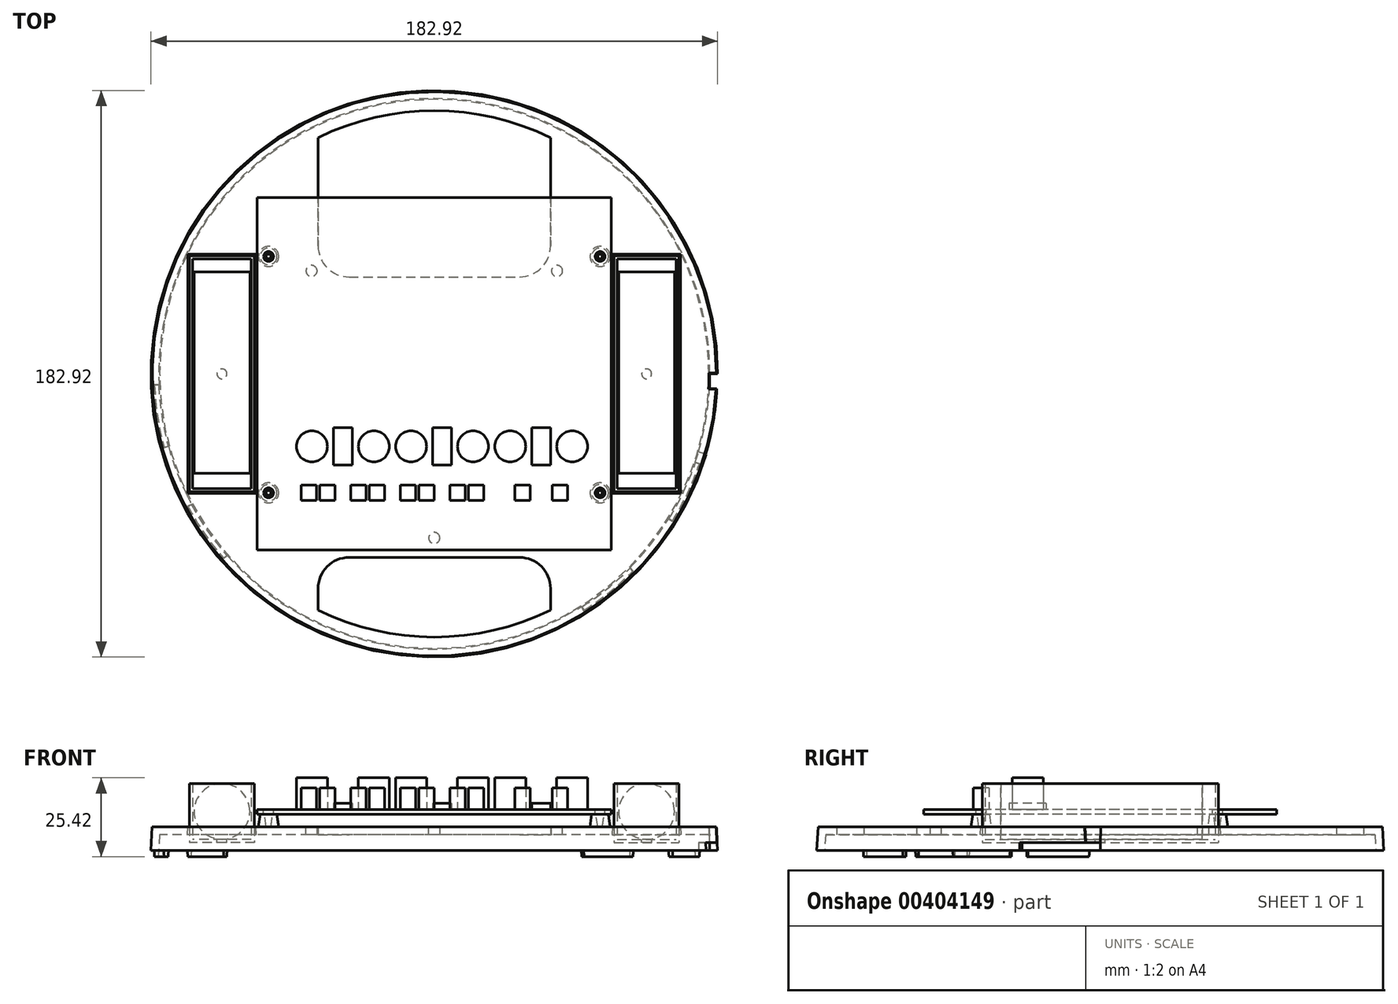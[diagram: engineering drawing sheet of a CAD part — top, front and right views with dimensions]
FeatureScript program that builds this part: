
annotation { "Feature Type Name" : "Feature", "Feature Type Description" : "" }
export const myFeature = defineFeature(function(context is Context, id is Id, definition is map)
    precondition{}
    {
        {
            assignVariable(context, id + "F0", {"name" : "h_env", "anyValue" : 230});
        }
        {
            var Q0;
            Q0=qCreatedBy(makeId("Top.planeOp"),FACE);
            var sketch = newSketch(context, id + "F1", { "sketchPlane" : qUnion([Q0])});
            skCircle(sketch, "E0", {"center": v(0, 0) * mm, "radius": 94 * mm});
            skSolve(sketch);
        }
        {
            var Q0;
            Q0=qCreatedBy(makeId("Top.planeOp"),FACE);
            cPlane(context, id + "F2", {"entities" : qUnion([Q0]), "cplaneType" : CPlaneType.OFFSET, "offset" : (getVariable(context, 'h_env')) * mm, "width" : 152.4 * mm, "height" : 152.4 * mm});
        }
        {
            var Q0;
            Q0=makeQuery(id+"F1.imprint","IMPRINT",FACE,{"disambiguationData":[TD([[makeQuery(id+"F1.imprint","IMPRINT",EDGE,{"derivedFrom":sQuery(id+"F1.wireOp",EDGE,"E0")}),1.0]])]});
            var Q1;
            Q1=sQuery(id+"F1.wireOp",EDGE,"E0");
            var Q2;
            Q2=qCreatedBy(id+"F2.planeOp",FACE);
            extrude(context, id + "F3", {"entities" : qUnion([Q0]), "bodyType" : ToolBodyType.SURFACE, "surfaceEntities" : qUnion([Q1]), "endBound" : BoundingType.UP_TO_SURFACE, "endBoundEntityFace" : qUnion([Q2]), "depth" : 25.4 * mm});
        }
        {
            var Q0;
            Q0=qCreatedBy(makeId("Right.planeOp"),FACE);
            var sketch = newSketch(context, id + "F4", { "sketchPlane" : qUnion([Q0])});
            skLineSegment(sketch, "E1", {"start": v(0, 0) * mm, "end": v(0, 230) * mm, "construction": true});
            skSolve(sketch);
        }
        {
            assignVariable(context, id + "F5", {"name" : "t", "anyValue" : 2.54});
        }
        {
            assignVariable(context, id + "F6", {"name" : "h_primary", "anyValue" : 19.05});
        }
        {
            assignVariable(context, id + "F7", {"name" : "draft", "anyValue" : 3});
        }
        {
            var Q0;
            Q0=qCreatedBy(id+"F2.planeOp",FACE);
            cPlane(context, id + "F8", {"entities" : qUnion([Q0]), "cplaneType" : CPlaneType.OFFSET, "offset" : (getVariable(context, 'h_primary')) * mm, "oppositeDirection" : true, "width" : 152.4 * mm, "height" : 152.4 * mm});
        }
        {
            var Q0;
            Q0=qCreatedBy(id+"F8.planeOp",FACE);
            var sketch = newSketch(context, id + "F9", { "sketchPlane" : qUnion([Q0])});
            skCircle(sketch, "E2", {"center": v(0, 0) * mm, "radius": 91.46 * mm});
            skSolve(sketch);
        }
        {
            var Q0;
            Q0=makeQuery(id+"F9.imprint","IMPRINT",FACE,{"disambiguationData":[TD([[makeQuery(id+"F9.imprint","IMPRINT",EDGE,{"derivedFrom":sQuery(id+"F9.wireOp",EDGE,"E2")}),1.0]])]});
            extrude(context, id + "F10", {"entities" : qUnion([Q0]), "depth" : (3 * getVariable(context, 't')) * mm, "hasDraft" : true, "draftAngle" : (getVariable(context, 'draft')) * degree, "draftPullDirection" : true});
        }
        {
            var Q0;
            Q0=makeQuery(id+"F10.opExtrude","CAP_FACE",FACE,{"disambiguationData":[OSD([sQuery(id+"F9.wireOp",EDGE,"E2")])],"isStart":true});
            shell(context, id + "F11", {"entities" : qUnion([Q0]), "thickness" : (getVariable(context, 't')) * mm});
        }
        {
            var Q0;
            Q0=makeQuery(id+"F10.opExtrude","CAP_FACE",FACE,{"disambiguationData":[OSD([sQuery(id+"F9.wireOp",EDGE,"E2")])],"isStart":true});
            var sketch = newSketch(context, id + "F12", { "sketchPlane" : qUnion([Q0])});
            skLineSegment(sketch, "E3", {"start": v(0, 0) * mm, "end": v(88.34, 23.67) * mm, "construction": true});
            skLineSegment(sketch, "E4", {"start": v(0, 0) * mm, "end": v(91.46, 0) * mm, "construction": true});
            skLineSegment(sketch, "E5", {"start": v(0, 0) * mm, "end": v(87.7, 25.98) * mm, "construction": true});
            skCircle(sketch, "E6.0", {"center": v(0, 0) * mm, "radius": 88.65 * mm});
            skArc(sketch, "E7", {"start": v(88.65, 0) * mm, "mid": v(87.73, 12.72) * mm, "end": v(85, 25.18) * mm});
            skLineSegment(sketch, "E8", {"start": v(87.7, 25.98) * mm, "end": v(85, 25.18) * mm});
            skLineSegment(sketch, "E9", {"start": v(91.46, 0) * mm, "end": v(88.65, 0) * mm});
            skSolve(sketch);
        }
        {
            var Q0;
            {var subQ0=sQuery(id+"F12.wireOp",EDGE,"E8");var subQ1=sQuery(id+"F9.wireOp",EDGE,"E2");var subQ2=makeQuery(id+"F10.opExtrude","CAP_EDGE",EDGE,{"disambiguationData":[OSD([subQ1])],"isStart":true});var subQ3=makeQuery(id+"F12.imprint","INTERSECT",VERTEX,{"derivedFrom":[subQ2,subQ0]});Q0=makeQuery(id+"F12.imprint","IMPRINT",FACE,{"disambiguationData":[TD([[makeQuery(id+"F12.imprint","IMPRINT",EDGE,{"disambiguationData":[TD([[subQ3,-1.0]])],"derivedFrom":subQ2}),-1.0]])]});}
            var Q1;
            {var subQ0=sQuery(id+"F12.wireOp",EDGE,"E8");var subQ1=sQuery(id+"F12.wireOp",EDGE,"E6.0");var subQ2=makeQuery(id+"F12.imprint","INTERSECT",VERTEX,{"derivedFrom":[subQ1,subQ0]});Q1=makeQuery(id+"F12.imprint","IMPRINT",FACE,{"disambiguationData":[TD([[makeQuery(id+"F12.imprint","IMPRINT",EDGE,{"disambiguationData":[TD([[subQ2,-1.0]])],"derivedFrom":subQ1}),1.0]])]});}
            extrude(context, id + "F13", {"entities" : qUnion([Q0, Q1]), "operationType" : NewBodyOperationType.REMOVE, "oppositeDirection" : true, "depth" : (getVariable(context, 't')) * mm});
        }
        {
            var Q0;
            Q0=makeQuery(id+"F13.boolean.opBoolean","COPY",FACE,{"derivedFrom":makeQuery(id+"F13.opExtrude","CAP_FACE",FACE,{"disambiguationData":[OSD([sQuery(id+"F9.wireOp",EDGE,"E2"),sQuery(id+"F12.wireOp",EDGE,"E6.0"),sQuery(id+"F12.wireOp",EDGE,"E8"),sQuery(id+"F12.wireOp",EDGE,"E9")])],"isStart":false})});
            var sketch = newSketch(context, id + "F14", { "sketchPlane" : qUnion([Q0])});
            skArc(sketch, "E10.0", {"start": v(91.33, 0) * mm, "mid": v(90.38, 13.1) * mm, "end": v(87.57, 25.94) * mm});
            skCircle(sketch, "E11.0", {"center": v(0, 0) * mm, "radius": 88.65 * mm});
            skLineSegment(sketch, "E12.0", {"start": v(91.33, 0) * mm, "end": v(88.65, 0) * mm});
            skPoint(sketch, "E13.orphan", {"position": v(88.78, 0) * mm});
            skLineSegment(sketch, "E14", {"start": v(0, 0) * mm, "end": v(91.33, 0) * mm, "construction": true});
            skLineSegment(sketch, "E15", {"start": v(0, 0) * mm, "end": v(91.2, 4.78) * mm, "construction": true});
            skLineSegment(sketch, "E16", {"start": v(91.2, 4.78) * mm, "end": v(88.53, 4.64) * mm});
            skSolve(sketch);
        }
        {
            var Q0;
            {var subQ0=sQuery(id+"F14.wireOp",EDGE,"E12.0");var subQ1=sQuery(id+"F14.wireOp",EDGE,"E10.0");var subQ2=makeQuery(id+"F14.imprint","INTERSECT",VERTEX,{"derivedFrom":[subQ1,subQ0]});Q0=makeQuery(id+"F14.imprint","IMPRINT",FACE,{"disambiguationData":[TD([[makeQuery(id+"F14.imprint","IMPRINT",EDGE,{"disambiguationData":[TD([[subQ2,-1.0]])],"derivedFrom":subQ1}),1.0]])]});}
            var Q1;
            Q1=makeQuery(id+"F10.opExtrude","CAP_FACE",FACE,{"disambiguationData":[OSD([sQuery(id+"F9.wireOp",EDGE,"E2")])],"isStart":false});
            extrude(context, id + "F15", {"entities" : qUnion([Q0]), "operationType" : NewBodyOperationType.REMOVE, "endBound" : BoundingType.UP_TO_SURFACE, "oppositeDirection" : true, "endBoundEntityFace" : qUnion([Q1]), "depth" : 25 * mm, "hasDraft" : true, "draftAngle" : 3 * degree});
        }
        {
            var Q0;
            Q0=makeQuery(id+"F9.imprint","IMPRINT",FACE,{"disambiguationData":[TD([[makeQuery(id+"F9.imprint","IMPRINT",EDGE,{"derivedFrom":sQuery(id+"F9.wireOp",EDGE,"E2")}),1.0]])]});
            var sketch = newSketch(context, id + "F16", { "sketchPlane" : qUnion([Q0])});
            skArc(sketch, "E17", {"start": v(-37.5, 76.28) * mm, "mid": v(0, 85) * mm, "end": v(37.5, 76.28) * mm});
            skLineSegment(sketch, "E18.bottom", {"start": v(-37.5, 76.28) * mm, "end": v(37.5, 76.28) * mm, "construction": true});
            skLineSegment(sketch, "E18.top", {"start": v(-27.5, 31.28) * mm, "end": v(27.5, 31.28) * mm});
            skLineSegment(sketch, "E18.left", {"start": v(-37.5, 76.28) * mm, "end": v(-37.5, 41.28) * mm});
            skLineSegment(sketch, "E18.right", {"start": v(37.5, 76.28) * mm, "end": v(37.5, 41.28) * mm});
            skPoint(sketch, "E19.visualSharp", {"position": v(37.5, 31.28) * mm});
            skArc(sketch, "E19.filletArc", {"start": v(27.5, 31.28) * mm, "mid": v(34.57, 34.2) * mm, "end": v(37.5, 41.28) * mm});
            skPoint(sketch, "E20.visualSharp", {"position": v(-37.5, 31.28) * mm});
            skArc(sketch, "E20.filletArc", {"start": v(-37.5, 41.28) * mm, "mid": v(-34.57, 34.2) * mm, "end": v(-27.5, 31.28) * mm});
            skArc(sketch, "E21", {"start": v(37.5, -76.28) * mm, "mid": v(0, -85) * mm, "end": v(-37.5, -76.28) * mm});
            skLineSegment(sketch, "E22.bottom", {"start": v(-37.5, -76.28) * mm, "end": v(37.5, -76.28) * mm, "construction": true});
            skLineSegment(sketch, "E22.top", {"start": v(-27.5, -59.28) * mm, "end": v(27.5, -59.28) * mm});
            skLineSegment(sketch, "E22.left", {"start": v(-37.5, -76.28) * mm, "end": v(-37.5, -69.28) * mm});
            skLineSegment(sketch, "E22.right", {"start": v(37.5, -76.28) * mm, "end": v(37.5, -69.28) * mm});
            skPoint(sketch, "E23.visualSharp", {"position": v(-37.5, -59.28) * mm});
            skArc(sketch, "E23.filletArc", {"start": v(-27.5, -59.28) * mm, "mid": v(-34.57, -62.2) * mm, "end": v(-37.5, -69.28) * mm});
            skPoint(sketch, "E24.visualSharp", {"position": v(37.5, -59.28) * mm});
            skArc(sketch, "E24.filletArc", {"start": v(37.5, -69.28) * mm, "mid": v(34.57, -62.2) * mm, "end": v(27.5, -59.28) * mm});
            skSolve(sketch);
        }
        {
            var Q0;
            Q0=qSketchRegion(id+"F16",true);
            var Q1;
            Q1=sQuery(id+"F16.wireOp",EDGE,"E18.bottom");
            var Q2;
            Q2=makeQuery(id+"F10.opExtrude","CAP_FACE",FACE,{"disambiguationData":[OSD([sQuery(id+"F9.wireOp",EDGE,"E2")])],"isStart":false});
            extrude(context, id + "F17", {"entities" : qUnion([Q0]), "operationType" : NewBodyOperationType.REMOVE, "surfaceEntities" : qUnion([Q1]), "endBound" : BoundingType.UP_TO_SURFACE, "endBoundEntityFace" : qUnion([Q2]), "depth" : 25 * mm});
        }
        {
            var Q0;
            Q0=qCreatedBy(id+"F8.planeOp",FACE);
            cPlane(context, id + "F18", {"entities" : qUnion([Q0]), "cplaneType" : CPlaneType.OFFSET, "offset" : (5 * getVariable(context, 't') - 1.08) * mm, "width" : 152.4 * mm, "height" : 152.4 * mm});
        }
        {
            assignVariable(context, id + "F19", {"name" : "h_pcb", "anyValue" : 1.6});
        }
        {
            var Q0;
            Q0=qCreatedBy(id+"F18.planeOp",FACE);
            var sketch = newSketch(context, id + "F20", { "sketchPlane" : qUnion([Q0])});
            skLineSegment(sketch, "E25.bottom", {"start": v(-57.15, 56.91) * mm, "end": v(57.15, 56.9) * mm});
            skLineSegment(sketch, "E25.top", {"start": v(-57.15, -56.9) * mm, "end": v(57.15, -56.91) * mm});
            skLineSegment(sketch, "E25.left", {"start": v(-57.15, 56.91) * mm, "end": v(-57.15, -56.91) * mm});
            skLineSegment(sketch, "E25.right", {"start": v(57.15, 56.91) * mm, "end": v(57.15, -56.91) * mm});
            skPoint(sketch, "E26", {"position": v(57.15, 0) * mm});
            skPoint(sketch, "E27", {"position": v(0, 56.9) * mm});
            skSolve(sketch);
        }
        {
            var Q0;
            Q0=makeQuery(id+"F20.imprint","IMPRINT",FACE,{"disambiguationData":[TD([[makeQuery(id+"F20.imprint","IMPRINT",EDGE,{"derivedFrom":sQuery(id+"F20.wireOp",EDGE,"E25.bottom")}),-1.0]])]});
            extrude(context, id + "F21", {"entities" : qUnion([Q0]), "depth" : (getVariable(context, 'h_pcb')) * mm});
        }
        {
            var Q0;
            Q0=makeQuery(id+"F21.opExtrude","CAP_FACE",FACE,{"disambiguationData":[OSD([sQuery(id+"F20.wireOp",EDGE,"E25.bottom"),sQuery(id+"F20.wireOp",EDGE,"E25.top"),sQuery(id+"F20.wireOp",EDGE,"E25.left"),sQuery(id+"F20.wireOp",EDGE,"E25.right")])],"isStart":false});
            var sketch = newSketch(context, id + "F22", { "sketchPlane" : qUnion([Q0])});
            skCircle(sketch, "E28", {"center": v(53.5, 37.9) * mm, "radius": 1.6 * mm});
            skCircle(sketch, "E29.0.1.0", {"center": v(53.5, -38.43) * mm, "radius": 1.6 * mm});
            skCircle(sketch, "E29.1.0.0", {"center": v(-53.5, 37.9) * mm, "radius": 1.6 * mm});
            skCircle(sketch, "E29.1.1.0", {"center": v(-53.5, -38.43) * mm, "radius": 1.6 * mm});
            skLineSegment(sketch, "E29.direction1", {"start": v(53.5, 37.9) * mm, "end": v(-53.5, 37.9) * mm, "construction": true});
            skLineSegment(sketch, "E29.direction2", {"start": v(53.5, 37.9) * mm, "end": v(53.5, -38.43) * mm, "construction": true});
            skSolve(sketch);
        }
        {
            var Q0;
            Q0=qSketchRegion(id+"F22",true);
            extrude(context, id + "F23", {"entities" : qUnion([Q0]), "operationType" : NewBodyOperationType.REMOVE, "endBound" : BoundingType.UP_TO_NEXT, "oppositeDirection" : true, "depth" : 25.4 * mm});
        }
        {
            var Q0;
            Q0=makeQuery(id+"F10.opExtrude","CAP_FACE",FACE,{"disambiguationData":[OSD([sQuery(id+"F9.wireOp",EDGE,"E2")])],"isStart":false});
            var sketch = newSketch(context, id + "F24", { "sketchPlane" : qUnion([Q0])});
            skCircle(sketch, "E30.0", {"center": v(53.5, 37.9) * mm, "radius": 1.6 * mm, "construction": true});
            skCircle(sketch, "E31.0", {"center": v(53.5, -38.43) * mm, "radius": 1.6 * mm, "construction": true});
            skCircle(sketch, "E32.0", {"center": v(-53.5, -38.43) * mm, "radius": 1.6 * mm, "construction": true});
            skCircle(sketch, "E33.0", {"center": v(-53.5, 37.9) * mm, "radius": 1.6 * mm, "construction": true});
            skCircle(sketch, "E34", {"center": v(53.5, 37.9) * mm, "radius": 3.25 * mm});
            skCircle(sketch, "E35", {"center": v(53.5, -38.43) * mm, "radius": 3.25 * mm});
            skCircle(sketch, "E36", {"center": v(-53.5, -38.43) * mm, "radius": 3.25 * mm});
            skCircle(sketch, "E37", {"center": v(-53.5, 37.9) * mm, "radius": 3.25 * mm});
            skCircle(sketch, "E38", {"center": v(53.5, 37.9) * mm, "radius": 0.75 * mm});
            skCircle(sketch, "E39", {"center": v(-53.5, 37.9) * mm, "radius": 0.75 * mm});
            skCircle(sketch, "E40", {"center": v(-53.5, -38.43) * mm, "radius": 0.75 * mm});
            skCircle(sketch, "E41", {"center": v(53.5, -38.43) * mm, "radius": 0.75 * mm});
            skSolve(sketch);
        }
        {
            var Q0;
            Q0=qSketchRegion(id+"F24",true);
            var Q1;
            Q1=sQuery(id+"F24.wireOp",EDGE,"D2eIxqeC-2rqa-4NXI-Nvdh-6eyWbRgn4P1Z");
            var Q2;
            Q2=makeQuery(id+"F21.opExtrude","CAP_FACE",FACE,{"disambiguationData":[OSD([sQuery(id+"F20.wireOp",EDGE,"E25.bottom"),sQuery(id+"F20.wireOp",EDGE,"E25.top"),sQuery(id+"F20.wireOp",EDGE,"E25.left"),sQuery(id+"F20.wireOp",EDGE,"E25.right")])],"isStart":true});
            extrude(context, id + "F25", {"entities" : qUnion([Q0]), "operationType" : NewBodyOperationType.ADD, "surfaceEntities" : qUnion([Q1]), "endBound" : BoundingType.UP_TO_SURFACE, "endBoundEntityFace" : qUnion([Q2]), "depth" : 25.4 * mm, "hasDraft" : true, "draftAngle" : 8 * degree, "draftPullDirection" : true});
        }
        {
            var Q0;
            {var subQ4=sQuery(id+"F9.wireOp",EDGE,"E2");Q0=makeQuery(id+"F25.boolean.opBoolean","SPLIT",FACE,{"disambiguationData":[TD([makeQuery(id+"F10.opExtrude","SWEPT_FACE",FACE,{"disambiguationData":[OSD([subQ4])]})])],"derivedFrom":makeQuery(id+"F10.opExtrude","CAP_FACE",FACE,{"disambiguationData":[OSD([subQ4])],"isStart":false})});}
            var sketch = newSketch(context, id + "F26", { "sketchPlane" : qUnion([Q0])});
            skCircle(sketch, "E42.0", {"center": v(0, 0) * mm, "radius": 94 * mm, "construction": true});
            skLineSegment(sketch, "E43", {"start": v(0, 0) * mm, "end": v(0, -94) * mm, "construction": true});
            skLineSegment(sketch, "E44", {"start": v(0, 0) * mm, "end": v(-72, 60.42) * mm, "construction": true});
            skCircle(sketch, "E45", {"center": v(0, -53) * mm, "radius": 1.8 * mm});
            skCircle(sketch, "E46", {"center": v(-39.61, 33.24) * mm, "radius": 1.8 * mm});
            skCircle(sketch, "E47.MirrorC", {"center": v(39.61, 33.24) * mm, "radius": 1.8 * mm});
            skSolve(sketch);
        }
        {
            var Q0;
            Q0=qSketchRegion(id+"F26",true);
            var Q1;
            {var subQ0=sQuery(id+"F9.wireOp",EDGE,"E2");Q1=makeQuery(id+"F11.opShell","OFFSET_FACE",FACE,{"disambiguationData":[OSD([subQ0]),TDD([makeQuery(id+"F10.opExtrude","CAP_FACE",FACE,{"disambiguationData":[OSD([subQ0])],"isStart":false})])]});}
            extrude(context, id + "F27", {"entities" : qUnion([Q0]), "operationType" : NewBodyOperationType.REMOVE, "endBound" : BoundingType.UP_TO_SURFACE, "oppositeDirection" : true, "endBoundEntityFace" : qUnion([Q1]), "depth" : 25 * mm});
        }
        {
            var Q0;
            Q0=makeQuery(id+"F21.opExtrude","CAP_FACE",FACE,{"disambiguationData":[OSD([sQuery(id+"F20.wireOp",EDGE,"E25.bottom"),sQuery(id+"F20.wireOp",EDGE,"E25.top"),sQuery(id+"F20.wireOp",EDGE,"E25.left"),sQuery(id+"F20.wireOp",EDGE,"E25.right")])],"isStart":false});
            var sketch = newSketch(context, id + "F28", { "sketchPlane" : qUnion([Q0])});
            skCircle(sketch, "E48.0", {"center": v(-53.5, -38.43) * mm, "radius": 1.6 * mm, "construction": true});
            skCircle(sketch, "E49.0", {"center": v(53.5, -38.43) * mm, "radius": 1.6 * mm, "construction": true});
            skLineSegment(sketch, "E50", {"start": v(-53.5, -38.43) * mm, "end": v(53.5, -38.43) * mm, "construction": true});
            skLineSegment(sketch, "E51.bottom", {"start": v(-38, -35.93) * mm, "end": v(-43, -35.93) * mm});
            skLineSegment(sketch, "E51.top", {"start": v(-38, -40.93) * mm, "end": v(-43, -40.93) * mm});
            skLineSegment(sketch, "E51.left", {"start": v(-38, -35.93) * mm, "end": v(-38, -40.93) * mm});
            skLineSegment(sketch, "E51.right", {"start": v(-43, -35.93) * mm, "end": v(-43, -40.93) * mm});
            skPoint(sketch, "E51.middle", {"position": v(-40.5, -38.43) * mm});
            skLineSegment(sketch, "E52.bottom", {"start": v(-37, -35.93) * mm, "end": v(-32, -35.93) * mm});
            skLineSegment(sketch, "E52.top", {"start": v(-37, -40.93) * mm, "end": v(-32, -40.93) * mm});
            skLineSegment(sketch, "E52.left", {"start": v(-37, -35.93) * mm, "end": v(-37, -40.93) * mm});
            skLineSegment(sketch, "E52.right", {"start": v(-32, -35.93) * mm, "end": v(-32, -40.93) * mm});
            skPoint(sketch, "E52.middle", {"position": v(-34.5, -38.43) * mm});
            skLineSegment(sketch, "E53.bottom", {"start": v(-27, -35.93) * mm, "end": v(-22, -35.93) * mm});
            skLineSegment(sketch, "E53.top", {"start": v(-27, -40.93) * mm, "end": v(-22, -40.93) * mm});
            skLineSegment(sketch, "E53.left", {"start": v(-27, -35.93) * mm, "end": v(-27, -40.93) * mm});
            skLineSegment(sketch, "E53.right", {"start": v(-22, -35.93) * mm, "end": v(-22, -40.93) * mm});
            skPoint(sketch, "E53.middle", {"position": v(-24.5, -38.43) * mm});
            skLineSegment(sketch, "E54.bottom", {"start": v(-21, -35.93) * mm, "end": v(-16, -35.93) * mm});
            skLineSegment(sketch, "E54.top", {"start": v(-21, -40.93) * mm, "end": v(-16, -40.93) * mm});
            skLineSegment(sketch, "E54.left", {"start": v(-21, -35.93) * mm, "end": v(-21, -40.93) * mm});
            skLineSegment(sketch, "E54.right", {"start": v(-16, -35.93) * mm, "end": v(-16, -40.93) * mm});
            skPoint(sketch, "E54.middle", {"position": v(-18.5, -38.43) * mm});
            skLineSegment(sketch, "E55.bottom", {"start": v(-11, -35.93) * mm, "end": v(-6, -35.93) * mm});
            skLineSegment(sketch, "E55.top", {"start": v(-11, -40.93) * mm, "end": v(-6, -40.93) * mm});
            skLineSegment(sketch, "E55.left", {"start": v(-11, -35.93) * mm, "end": v(-11, -40.93) * mm});
            skLineSegment(sketch, "E55.right", {"start": v(-6, -35.93) * mm, "end": v(-6, -40.93) * mm});
            skPoint(sketch, "E55.middle", {"position": v(-8.5, -38.43) * mm});
            skLineSegment(sketch, "E56.bottom", {"start": v(-5, -35.93) * mm, "end": v(0, -35.93) * mm});
            skLineSegment(sketch, "E56.top", {"start": v(-5, -40.93) * mm, "end": v(0, -40.93) * mm});
            skLineSegment(sketch, "E56.left", {"start": v(-5, -35.93) * mm, "end": v(-5, -40.93) * mm});
            skLineSegment(sketch, "E56.right", {"start": v(0, -35.93) * mm, "end": v(0, -40.93) * mm});
            skPoint(sketch, "E56.middle", {"position": v(-2.5, -38.43) * mm});
            skLineSegment(sketch, "E57.bottom", {"start": v(5, -35.93) * mm, "end": v(10, -35.93) * mm});
            skLineSegment(sketch, "E57.top", {"start": v(5, -40.93) * mm, "end": v(10, -40.93) * mm});
            skLineSegment(sketch, "E57.left", {"start": v(5, -35.93) * mm, "end": v(5, -40.93) * mm});
            skLineSegment(sketch, "E57.right", {"start": v(10, -35.93) * mm, "end": v(10, -40.93) * mm});
            skPoint(sketch, "E57.middle", {"position": v(7.5, -38.43) * mm});
            skLineSegment(sketch, "E58.bottom", {"start": v(11, -35.93) * mm, "end": v(16, -35.93) * mm});
            skLineSegment(sketch, "E58.top", {"start": v(11, -40.93) * mm, "end": v(16, -40.93) * mm});
            skLineSegment(sketch, "E58.left", {"start": v(11, -35.93) * mm, "end": v(11, -40.93) * mm});
            skLineSegment(sketch, "E58.right", {"start": v(16, -35.93) * mm, "end": v(16, -40.93) * mm});
            skPoint(sketch, "E58.middle", {"position": v(13.5, -38.43) * mm});
            skLineSegment(sketch, "E59.bottom", {"start": v(26, -35.93) * mm, "end": v(31, -35.93) * mm});
            skLineSegment(sketch, "E59.top", {"start": v(26, -40.93) * mm, "end": v(31, -40.93) * mm});
            skLineSegment(sketch, "E59.left", {"start": v(26, -35.93) * mm, "end": v(26, -40.93) * mm});
            skLineSegment(sketch, "E59.right", {"start": v(31, -35.93) * mm, "end": v(31, -40.93) * mm});
            skPoint(sketch, "E59.middle", {"position": v(28.5, -38.43) * mm});
            skLineSegment(sketch, "E60.bottom", {"start": v(38, -35.93) * mm, "end": v(43, -35.93) * mm});
            skLineSegment(sketch, "E60.top", {"start": v(38, -40.93) * mm, "end": v(43, -40.93) * mm});
            skLineSegment(sketch, "E60.left", {"start": v(38, -35.93) * mm, "end": v(38, -40.93) * mm});
            skLineSegment(sketch, "E60.right", {"start": v(43, -35.93) * mm, "end": v(43, -40.93) * mm});
            skPoint(sketch, "E60.middle", {"position": v(40.5, -38.43) * mm});
            skSolve(sketch);
        }
        {
            var Q0;
            Q0=qSketchRegion(id+"F28",true);
            extrude(context, id + "F29", {"entities" : qUnion([Q0]), "operationType" : NewBodyOperationType.ADD, "depth" : 7 * mm});
        }
        {
            var Q0;
            Q0=makeQuery(id+"F21.opExtrude","CAP_FACE",FACE,{"disambiguationData":[OSD([sQuery(id+"F20.wireOp",EDGE,"E25.bottom"),sQuery(id+"F20.wireOp",EDGE,"E25.top"),sQuery(id+"F20.wireOp",EDGE,"E25.left"),sQuery(id+"F20.wireOp",EDGE,"E25.right")])],"isStart":false});
            var sketch = newSketch(context, id + "F30", { "sketchPlane" : qUnion([Q0])});
            skLineSegment(sketch, "E61.bottom", {"start": v(-26.5, -17.43) * mm, "end": v(-32.5, -17.43) * mm});
            skLineSegment(sketch, "E61.top", {"start": v(-26.5, -29.43) * mm, "end": v(-32.5, -29.43) * mm});
            skLineSegment(sketch, "E61.left", {"start": v(-26.5, -17.43) * mm, "end": v(-26.5, -29.43) * mm});
            skLineSegment(sketch, "E61.right", {"start": v(-32.5, -17.43) * mm, "end": v(-32.5, -29.43) * mm});
            skPoint(sketch, "E61.middle", {"position": v(-29.5, -23.43) * mm});
            skLineSegment(sketch, "E62.bottom", {"start": v(-0.5, -17.43) * mm, "end": v(5.5, -17.43) * mm});
            skLineSegment(sketch, "E62.top", {"start": v(-0.5, -29.43) * mm, "end": v(5.5, -29.43) * mm});
            skLineSegment(sketch, "E62.left", {"start": v(-0.5, -17.43) * mm, "end": v(-0.5, -29.43) * mm});
            skLineSegment(sketch, "E62.right", {"start": v(5.5, -17.43) * mm, "end": v(5.5, -29.43) * mm});
            skPoint(sketch, "E62.middle", {"position": v(2.5, -23.43) * mm});
            skLineSegment(sketch, "E63.bottom", {"start": v(31.5, -17.43) * mm, "end": v(37.5, -17.43) * mm});
            skLineSegment(sketch, "E63.top", {"start": v(31.5, -29.43) * mm, "end": v(37.5, -29.43) * mm});
            skLineSegment(sketch, "E63.left", {"start": v(31.5, -17.43) * mm, "end": v(31.5, -29.43) * mm});
            skLineSegment(sketch, "E63.right", {"start": v(37.5, -17.43) * mm, "end": v(37.5, -29.43) * mm});
            skPoint(sketch, "E63.middle", {"position": v(34.5, -23.43) * mm});
            skCircle(sketch, "E64.0", {"center": v(-53.5, -38.43) * mm, "radius": 1.6 * mm, "construction": true});
            skCircle(sketch, "E65.0", {"center": v(53.5, -38.43) * mm, "radius": 1.6 * mm, "construction": true});
            skLineSegment(sketch, "E66", {"start": v(53.5, -38.43) * mm, "end": v(-53.5, -38.43) * mm, "construction": true});
            skSolve(sketch);
        }
        {
            var Q0;
            Q0=qSketchRegion(id+"F30",true);
            extrude(context, id + "F31", {"entities" : qUnion([Q0]), "operationType" : NewBodyOperationType.ADD, "depth" : 2 * mm});
        }
        {
            var Q0;
            Q0=makeQuery(id+"F21.opExtrude","CAP_FACE",FACE,{"disambiguationData":[OSD([sQuery(id+"F20.wireOp",EDGE,"E25.bottom"),sQuery(id+"F20.wireOp",EDGE,"E25.top"),sQuery(id+"F20.wireOp",EDGE,"E25.left"),sQuery(id+"F20.wireOp",EDGE,"E25.right")])],"isStart":false});
            var sketch = newSketch(context, id + "F32", { "sketchPlane" : qUnion([Q0])});
            skLineSegment(sketch, "E67.0.0", {"start": v(-26.5, -29.43) * mm, "end": v(-26.5, -17.43) * mm, "construction": true});
            skLineSegment(sketch, "E67.0.1", {"start": v(-26.5, -17.43) * mm, "end": v(-32.5, -17.43) * mm, "construction": true});
            skLineSegment(sketch, "E67.0.2", {"start": v(-32.5, -17.43) * mm, "end": v(-32.5, -29.43) * mm, "construction": true});
            skLineSegment(sketch, "E67.0.3", {"start": v(-32.5, -29.43) * mm, "end": v(-26.5, -29.43) * mm, "construction": true});
            skLineSegment(sketch, "E68.0.0", {"start": v(5.5, -17.43) * mm, "end": v(-0.5, -17.43) * mm, "construction": true});
            skLineSegment(sketch, "E68.0.1", {"start": v(-0.5, -17.43) * mm, "end": v(-0.5, -29.43) * mm, "construction": true});
            skLineSegment(sketch, "E68.0.2", {"start": v(-0.5, -29.43) * mm, "end": v(5.5, -29.43) * mm, "construction": true});
            skLineSegment(sketch, "E68.0.3", {"start": v(5.5, -29.43) * mm, "end": v(5.5, -17.43) * mm, "construction": true});
            skLineSegment(sketch, "E69.0.0", {"start": v(37.5, -17.43) * mm, "end": v(31.5, -17.43) * mm, "construction": true});
            skLineSegment(sketch, "E69.0.1", {"start": v(31.5, -17.43) * mm, "end": v(31.5, -29.43) * mm, "construction": true});
            skLineSegment(sketch, "E69.0.2", {"start": v(31.5, -29.43) * mm, "end": v(37.5, -29.43) * mm, "construction": true});
            skLineSegment(sketch, "E69.0.3", {"start": v(37.5, -29.43) * mm, "end": v(37.5, -17.43) * mm, "construction": true});
            skLineSegment(sketch, "E70", {"start": v(-29.5, -17.43) * mm, "end": v(-29.5, -29.43) * mm, "construction": true});
            skLineSegment(sketch, "E71", {"start": v(-26.5, -23.43) * mm, "end": v(-32.5, -23.43) * mm, "construction": true});
            skCircle(sketch, "E72", {"center": v(-39.5, -23.43) * mm, "radius": 5 * mm});
            skCircle(sketch, "E73", {"center": v(-19.5, -23.43) * mm, "radius": 5 * mm});
            skPoint(sketch, "E73.centerSnap0", {"position": v(-29.5, -23.43) * mm});
            skLineSegment(sketch, "E74", {"start": v(2.5, -17.43) * mm, "end": v(2.5, -29.43) * mm, "construction": true});
            skLineSegment(sketch, "E75", {"start": v(-0.5, -23.43) * mm, "end": v(5.5, -23.43) * mm, "construction": true});
            skLineSegment(sketch, "E76", {"start": v(31.5, -23.43) * mm, "end": v(37.5, -23.43) * mm, "construction": true});
            skLineSegment(sketch, "E77", {"start": v(34.5, -17.43) * mm, "end": v(34.5, -29.43) * mm, "construction": true});
            skCircle(sketch, "E78", {"center": v(-7.5, -23.43) * mm, "radius": 5 * mm});
            skCircle(sketch, "E79", {"center": v(12.5, -23.43) * mm, "radius": 5 * mm});
            skPoint(sketch, "E79.centerSnap0", {"position": v(2.5, -23.43) * mm});
            skCircle(sketch, "E80", {"center": v(24.5, -23.43) * mm, "radius": 5 * mm});
            skCircle(sketch, "E81", {"center": v(44.5, -23.43) * mm, "radius": 5 * mm});
            skPoint(sketch, "E81.centerSnap0", {"position": v(34.5, -23.43) * mm});
            skLineSegment(sketch, "E82", {"start": v(-29.5, -23.43) * mm, "end": v(-39.5, -23.43) * mm, "construction": true});
            skLineSegment(sketch, "E83", {"start": v(-29.5, -23.43) * mm, "end": v(-19.5, -23.43) * mm, "construction": true});
            skLineSegment(sketch, "E84", {"start": v(-7.5, -23.43) * mm, "end": v(2.5, -23.43) * mm, "construction": true});
            skLineSegment(sketch, "E85", {"start": v(2.5, -23.43) * mm, "end": v(12.5, -23.43) * mm, "construction": true});
            skLineSegment(sketch, "E86", {"start": v(24.5, -23.43) * mm, "end": v(34.5, -23.43) * mm, "construction": true});
            skLineSegment(sketch, "E87", {"start": v(34.5, -23.43) * mm, "end": v(44.5, -23.43) * mm, "construction": true});
            skSolve(sketch);
        }
        {
            var Q0;
            Q0=qSketchRegion(id+"F32",true);
            extrude(context, id + "F33", {"entities" : qUnion([Q0]), "operationType" : NewBodyOperationType.ADD, "depth" : 10.2 * mm});
        }
        {
            var Q0;
            Q0=makeQuery(id+"F9.imprint","IMPRINT",FACE,{"disambiguationData":[TD([[makeQuery(id+"F9.imprint","IMPRINT",EDGE,{"derivedFrom":sQuery(id+"F9.wireOp",EDGE,"E2")}),1.0]])]});
            var sketch = newSketch(context, id + "F34", { "sketchPlane" : qUnion([Q0])});
            skLineSegment(sketch, "E88.0", {"start": v(57.15, 56.9) * mm, "end": v(57.15, -56.91) * mm, "construction": true});
            skLineSegment(sketch, "E89.bottom", {"start": v(57.15, -39) * mm, "end": v(79.9, -39) * mm});
            skLineSegment(sketch, "E89.top", {"start": v(57.15, 39) * mm, "end": v(79.9, 39) * mm});
            skLineSegment(sketch, "E89.left", {"start": v(57.15, -39) * mm, "end": v(57.15, 39) * mm});
            skLineSegment(sketch, "E89.right", {"start": v(79.9, -39) * mm, "end": v(79.9, 39) * mm});
            skPoint(sketch, "E90", {"position": v(57.15, 0) * mm});
            skArc(sketch, "E91.0", {"start": v(44.46, -77) * mm, "mid": v(69.83, -55.05) * mm, "end": v(85.25, -25.25) * mm, "construction": true});
            skArc(sketch, "E92.0", {"start": v(88.92, 0) * mm, "mid": v(82.59, 32.95) * mm, "end": v(64.5, 61.2) * mm, "construction": true});
            skLineSegment(sketch, "E93.MirrorCS", {"start": v(-79.9, -39) * mm, "end": v(-79.9, 39) * mm});
            skLineSegment(sketch, "E94.MirrorCS", {"start": v(-57.15, 39) * mm, "end": v(-79.9, 39) * mm});
            skLineSegment(sketch, "E95.MirrorCS", {"start": v(-57.15, 56.9) * mm, "end": v(-57.15, -56.91) * mm, "construction": true});
            skLineSegment(sketch, "E96.MirrorCS", {"start": v(-57.15, -39) * mm, "end": v(-79.9, -39) * mm});
            skLineSegment(sketch, "E97.MirrorCS", {"start": v(-57.15, -39) * mm, "end": v(-57.15, 39) * mm});
            skSolve(sketch);
        }
        {
            var Q0;
            Q0=qSketchRegion(id+"F34",true);
            var Q1;
            {var subQ4=sQuery(id+"F9.wireOp",EDGE,"E2");Q1=makeQuery(id+"F25.boolean.opBoolean","SPLIT",FACE,{"disambiguationData":[TD([makeQuery(id+"F10.opExtrude","SWEPT_FACE",FACE,{"disambiguationData":[OSD([subQ4])]})])],"derivedFrom":makeQuery(id+"F10.opExtrude","CAP_FACE",FACE,{"disambiguationData":[OSD([subQ4])],"isStart":false})});}
            extrude(context, id + "F35", {"entities" : qUnion([Q0]), "operationType" : NewBodyOperationType.REMOVE, "endBound" : BoundingType.UP_TO_SURFACE, "endBoundEntityFace" : qUnion([Q1]), "depth" : 25 * mm, "hasDraft" : true, "draftAngle" : 3 * degree, "draftPullDirection" : true});
        }
        {
            var Q0;
            {var subQ4=sQuery(id+"F9.wireOp",EDGE,"E2");Q0=makeQuery(id+"F25.boolean.opBoolean","SPLIT",FACE,{"disambiguationData":[TD([makeQuery(id+"F10.opExtrude","SWEPT_FACE",FACE,{"disambiguationData":[OSD([subQ4])]})])],"derivedFrom":makeQuery(id+"F10.opExtrude","CAP_FACE",FACE,{"disambiguationData":[OSD([subQ4])],"isStart":false})});}
            var sketch = newSketch(context, id + "F36", { "sketchPlane" : qUnion([Q0])});
            skLineSegment(sketch, "E98.0", {"start": v(-57.55, -38.6) * mm, "end": v(-79.5, -38.6) * mm, "construction": true});
            skLineSegment(sketch, "E99.0", {"start": v(-57.55, -38.6) * mm, "end": v(-57.55, 38.6) * mm, "construction": true});
            skLineSegment(sketch, "E100.0", {"start": v(-79.5, -38.6) * mm, "end": v(-79.5, 38.6) * mm, "construction": true});
            skLineSegment(sketch, "E101.0", {"start": v(-57.55, 38.6) * mm, "end": v(-79.5, 38.6) * mm, "construction": true});
            skLineSegment(sketch, "E102.0", {"start": v(-58.05, -38.1) * mm, "end": v(-58.05, 38.1) * mm});
            skLineSegment(sketch, "E102.1", {"start": v(-58.05, -38.1) * mm, "end": v(-79, -38.1) * mm});
            skLineSegment(sketch, "E102.2", {"start": v(-79, -38.1) * mm, "end": v(-79, 38.1) * mm});
            skLineSegment(sketch, "E102.3", {"start": v(-58.05, 38.1) * mm, "end": v(-79, 38.1) * mm});
            skLineSegment(sketch, "E103.MirrorCS", {"start": v(58.05, -38.1) * mm, "end": v(58.05, 38.1) * mm});
            skLineSegment(sketch, "E104.MirrorCS", {"start": v(58.05, -38.1) * mm, "end": v(79, -38.1) * mm});
            skLineSegment(sketch, "E105.MirrorCS", {"start": v(79, -38.1) * mm, "end": v(79, 38.1) * mm});
            skLineSegment(sketch, "E106.MirrorCS", {"start": v(58.05, 38.1) * mm, "end": v(79, 38.1) * mm});
            skSolve(sketch);
        }
        {
            var Q0;
            Q0=qSketchRegion(id+"F36",true);
            extrude(context, id + "F37", {"entities" : qUnion([Q0]), "depth" : 14 * mm, "hasSecondDirection" : true, "secondDirectionOppositeDirection" : true, "secondDirectionDepth" : (2 * getVariable(context, 't')) * mm});
        }
        {
            var Q0;
            Q0=makeQuery(id+"F37.opExtrude","CAP_FACE",FACE,{"disambiguationData":[OSD([sQuery(id+"F36.wireOp",EDGE,"E102.0"),sQuery(id+"F36.wireOp",EDGE,"E102.1"),sQuery(id+"F36.wireOp",EDGE,"E102.2"),sQuery(id+"F36.wireOp",EDGE,"E102.3")])],"isStart":false});
            var Q1;
            Q1=makeQuery(id+"F37.opExtrude","CAP_FACE",FACE,{"disambiguationData":[OSD([sQuery(id+"F36.wireOp",EDGE,"E103.MirrorCS"),sQuery(id+"F36.wireOp",EDGE,"E104.MirrorCS"),sQuery(id+"F36.wireOp",EDGE,"E105.MirrorCS"),sQuery(id+"F36.wireOp",EDGE,"E106.MirrorCS")])],"isStart":false});
            shell(context, id + "F38", {"entities" : qUnion([Q0, Q1]), "thickness" : 1 * mm});
        }
        {
            var Q0;
            Q0=makeQuery(id+"F38.opShell","OFFSET_FACE",FACE,{"disambiguationData":[OSD([sQuery(id+"F36.wireOp",EDGE,"E102.0"),sQuery(id+"F36.wireOp",EDGE,"E102.1"),sQuery(id+"F36.wireOp",EDGE,"E102.2"),sQuery(id+"F36.wireOp",EDGE,"E102.3")])]});
            var sketch = newSketch(context, id + "F39", { "sketchPlane" : qUnion([Q0])});
            skLineSegment(sketch, "E107", {"start": v(-68.53, -37.1) * mm, "end": v(-68.53, 37.1) * mm, "construction": true});
            skLineSegment(sketch, "E108", {"start": v(-59.05, 0) * mm, "end": v(-78, 0) * mm, "construction": true});
            skCircle(sketch, "E109", {"center": v(-68.53, 0) * mm, "radius": 1.6 * mm});
            skCircle(sketch, "E110.MirrorC", {"center": v(68.53, 0) * mm, "radius": 1.6 * mm});
            skLineSegment(sketch, "E111", {"start": v(0, 0) * mm, "end": v(68.53, 0) * mm, "construction": true});
            skSolve(sketch);
        }
        {
            var Q0;
            Q0=qSketchRegion(id+"F39",true);
            var Q1;
            Q1=makeQuery(id+"F37.opExtrude","CAP_FACE",FACE,{"disambiguationData":[OSD([sQuery(id+"F36.wireOp",EDGE,"E103.MirrorCS"),sQuery(id+"F36.wireOp",EDGE,"E104.MirrorCS"),sQuery(id+"F36.wireOp",EDGE,"E105.MirrorCS"),sQuery(id+"F36.wireOp",EDGE,"E106.MirrorCS")])],"isStart":true});
            extrude(context, id + "F40", {"entities" : qUnion([Q0]), "operationType" : NewBodyOperationType.REMOVE, "endBound" : BoundingType.UP_TO_SURFACE, "oppositeDirection" : true, "endBoundEntityFace" : qUnion([Q1]), "depth" : 25 * mm});
        }
        {
            var Q0;
            Q0=makeQuery(id+"F38.opShell","OFFSET_FACE",FACE,{"disambiguationData":[OSD([sQuery(id+"F36.wireOp",EDGE,"E102.1")])]});
            var sketch = newSketch(context, id + "F41", { "sketchPlane" : qUnion([Q0])});
            skLineSegment(sketch, "E112", {"start": v(68.53, 232.57) * mm, "end": v(68.53, 214.49) * mm, "construction": true});
            skLineSegment(sketch, "E113", {"start": v(59.05, 223.53) * mm, "end": v(78, 223.53) * mm, "construction": true});
            skCircle(sketch, "E114", {"center": v(68.53, 223.53) * mm, "radius": 9 * mm});
            skCircle(sketch, "E115.MirrorC", {"center": v(-68.53, 223.53) * mm, "radius": 9 * mm});
            skSolve(sketch);
        }
        {
            var Q0;
            Q0=qSketchRegion(id+"F41",true);
            extrude(context, id + "F42", {"entities" : qUnion([Q0]), "depth" : 70 * mm, "hasSecondDirection" : true, "secondDirectionOppositeDirection" : false, "secondDirectionDepth" : 5 * mm});
        }
        {
            var Q0;
            Q0=makeQuery(id+"F9.imprint","IMPRINT",FACE,{"disambiguationData":[TD([[makeQuery(id+"F9.imprint","IMPRINT",EDGE,{"derivedFrom":sQuery(id+"F9.wireOp",EDGE,"E2")}),1.0]])]});
            var sketch = newSketch(context, id + "F43", { "sketchPlane" : qUnion([Q0])});
            skArc(sketch, "E116.0", {"start": v(44.46, -77) * mm, "mid": v(45.96, -76.12) * mm, "end": v(47.45, -75.2) * mm, "construction": true});
            skArc(sketch, "E117.0", {"start": v(-79.9, -39) * mm, "mid": v(-79.13, -40.55) * mm, "end": v(-78.33, -42.09) * mm, "construction": true});
            skArc(sketch, "E118.0", {"start": v(-88.92, 0) * mm, "mid": v(-88.9, -1.75) * mm, "end": v(-88.85, -3.5) * mm, "construction": true});
            skArc(sketch, "E119.0", {"start": v(79.9, -39) * mm, "mid": v(82.22, -33.86) * mm, "end": v(84.2, -28.58) * mm});
            skLineSegment(sketch, "E120", {"start": v(0, 0) * mm, "end": v(44.46, -77) * mm, "construction": true});
            skLineSegment(sketch, "E121", {"start": v(0, 0) * mm, "end": v(85.25, -25.25) * mm, "construction": true});
            skLineSegment(sketch, "E122", {"start": v(0, 0) * mm, "end": v(47.45, -75.2) * mm, "construction": true});
            skLineSegment(sketch, "E123", {"start": v(0, 0) * mm, "end": v(84.2, -28.58) * mm, "construction": true});
            skLineSegment(sketch, "E124", {"start": v(0, 0) * mm, "end": v(64.95, -64.39) * mm, "construction": true});
            skLineSegment(sketch, "E125", {"start": v(0, 0) * mm, "end": v(77.77, -48.13) * mm, "construction": true});
            skLineSegment(sketch, "E126", {"start": v(47.45, -75.2) * mm, "end": v(48.27, -76.5) * mm});
            skLineSegment(sketch, "E127", {"start": v(63.15, -62.6) * mm, "end": v(64.24, -63.69) * mm});
            skLineSegment(sketch, "E128", {"start": v(75.61, -46.79) * mm, "end": v(76.92, -47.6) * mm});
            skLineSegment(sketch, "E129", {"start": v(84.2, -28.58) * mm, "end": v(85.66, -29.08) * mm});
            skLineSegment(sketch, "E130", {"start": v(0, 0) * mm, "end": v(-64.5, -61.2) * mm, "construction": true});
            skLineSegment(sketch, "E131", {"start": v(0, 0) * mm, "end": v(-88.92, 0) * mm, "construction": true});
            skLineSegment(sketch, "E132", {"start": v(0, 0) * mm, "end": v(-80.57, -43.29) * mm, "construction": true});
            skLineSegment(sketch, "E133", {"start": v(0, 0) * mm, "end": v(-88.24, -24.06) * mm, "construction": true});
            skLineSegment(sketch, "E134", {"start": v(0, 0) * mm, "end": v(-68.76, -60.3) * mm, "construction": true});
            skLineSegment(sketch, "E135", {"start": v(0, 0) * mm, "end": v(-91.39, -3.6) * mm, "construction": true});
            skLineSegment(sketch, "E136", {"start": v(-68.76, -60.3) * mm, "end": v(-68.01, -59.64) * mm, "construction": true});
            skLineSegment(sketch, "E137", {"start": v(-80.57, -43.29) * mm, "end": v(-79.69, -42.82) * mm, "construction": true});
            skLineSegment(sketch, "E138", {"start": v(-88.24, -24.06) * mm, "end": v(-87.27, -23.8) * mm, "construction": true});
            skLineSegment(sketch, "E139", {"start": v(-91.39, -3.6) * mm, "end": v(-90.4, -3.55) * mm, "construction": true});
            skArc(sketch, "E140", {"start": v(-68.76, -60.3) * mm, "mid": v(-13.12, -90.51) * mm, "end": v(48.8, -77.35) * mm, "construction": true});
            skArc(sketch, "E141", {"start": v(-80.57, -43.29) * mm, "mid": v(-75.15, -52.13) * mm, "end": v(-68.76, -60.3) * mm, "construction": true});
            skArc(sketch, "E142", {"start": v(-88.24, -24.06) * mm, "mid": v(-84.95, -33.9) * mm, "end": v(-80.57, -43.29) * mm, "construction": true});
            skArc(sketch, "E143", {"start": v(-91.39, -3.6) * mm, "mid": v(-90.4, -13.91) * mm, "end": v(-88.24, -24.06) * mm, "construction": true});
            skArc(sketch, "E144", {"start": v(48.8, -77.35) * mm, "mid": v(57.25, -71.33) * mm, "end": v(64.95, -64.39) * mm, "construction": true});
            skArc(sketch, "E145", {"start": v(64.95, -64.39) * mm, "mid": v(71.83, -56.62) * mm, "end": v(77.77, -48.13) * mm, "construction": true});
            skArc(sketch, "E146", {"start": v(77.77, -48.13) * mm, "mid": v(82.72, -39.01) * mm, "end": v(86.6, -29.4) * mm, "construction": true});
            skArc(sketch, "E147", {"start": v(86.6, -29.4) * mm, "mid": v(13.12, 90.51) * mm, "end": v(-91.39, -3.6) * mm, "construction": true});
            skArc(sketch, "E148", {"start": v(-85.79, -23.39) * mm, "mid": v(-83.21, -31.33) * mm, "end": v(-79.9, -39) * mm, "construction": true});
            skArc(sketch, "E149", {"start": v(-66.85, -58.63) * mm, "mid": v(-65.69, -59.93) * mm, "end": v(-64.5, -61.2) * mm, "construction": true});
            skArc(sketch, "E150", {"start": v(-78.33, -42.09) * mm, "mid": v(-73.06, -50.68) * mm, "end": v(-66.85, -58.63) * mm});
            skArc(sketch, "E151", {"start": v(-88.85, -3.5) * mm, "mid": v(-87.88, -13.53) * mm, "end": v(-85.79, -23.39) * mm});
            skArc(sketch, "E152", {"start": v(47.45, -75.2) * mm, "mid": v(55.65, -69.34) * mm, "end": v(63.15, -62.6) * mm});
            skArc(sketch, "E153", {"start": v(63.15, -62.6) * mm, "mid": v(69.83, -55.05) * mm, "end": v(75.61, -46.79) * mm, "construction": true});
            skArc(sketch, "E154", {"start": v(75.61, -46.79) * mm, "mid": v(77.86, -42.95) * mm, "end": v(79.9, -39) * mm});
            skArc(sketch, "E155", {"start": v(84.2, -28.58) * mm, "mid": v(84.74, -26.92) * mm, "end": v(85.25, -25.25) * mm, "construction": true});
            skArc(sketch, "E156.0", {"start": v(48.27, -76.5) * mm, "mid": v(56.62, -70.55) * mm, "end": v(64.24, -63.69) * mm});
            skArc(sketch, "E157.0", {"start": v(76.92, -47.6) * mm, "mid": v(81.82, -38.59) * mm, "end": v(85.66, -29.08) * mm});
            skArc(sketch, "E158.0", {"start": v(-79.69, -42.82) * mm, "mid": v(-74.33, -51.56) * mm, "end": v(-68.01, -59.64) * mm});
            skArc(sketch, "E159.0", {"start": v(-90.4, -3.55) * mm, "mid": v(-89.4, -13.76) * mm, "end": v(-87.27, -23.8) * mm});
            skLineSegment(sketch, "E160", {"start": v(76.92, -47.6) * mm, "end": v(77.77, -48.13) * mm, "construction": true});
            skLineSegment(sketch, "E161", {"start": v(85.66, -29.08) * mm, "end": v(86.6, -29.4) * mm, "construction": true});
            skLineSegment(sketch, "E162", {"start": v(64.24, -63.69) * mm, "end": v(64.95, -64.39) * mm, "construction": true});
            skLineSegment(sketch, "E163", {"start": v(48.27, -76.5) * mm, "end": v(48.8, -77.35) * mm, "construction": true});
            skLineSegment(sketch, "E164", {"start": v(-68.01, -59.64) * mm, "end": v(-66.85, -58.63) * mm});
            skLineSegment(sketch, "E165", {"start": v(-79.69, -42.82) * mm, "end": v(-78.33, -42.09) * mm});
            skLineSegment(sketch, "E166", {"start": v(-87.27, -23.8) * mm, "end": v(-85.79, -23.39) * mm});
            skLineSegment(sketch, "E167", {"start": v(-90.4, -3.55) * mm, "end": v(-88.85, -3.5) * mm});
            skSolve(sketch);
        }
        {
            var Q0;
            Q0=qSketchRegion(id+"F43",true);
            extrude(context, id + "F44", {"entities" : qUnion([Q0]), "operationType" : NewBodyOperationType.ADD, "oppositeDirection" : true, "depth" : 2 * mm, "hasDraft" : true, "draftAngle" : 3 * degree, "draftPullDirection" : true});
        }
    });
